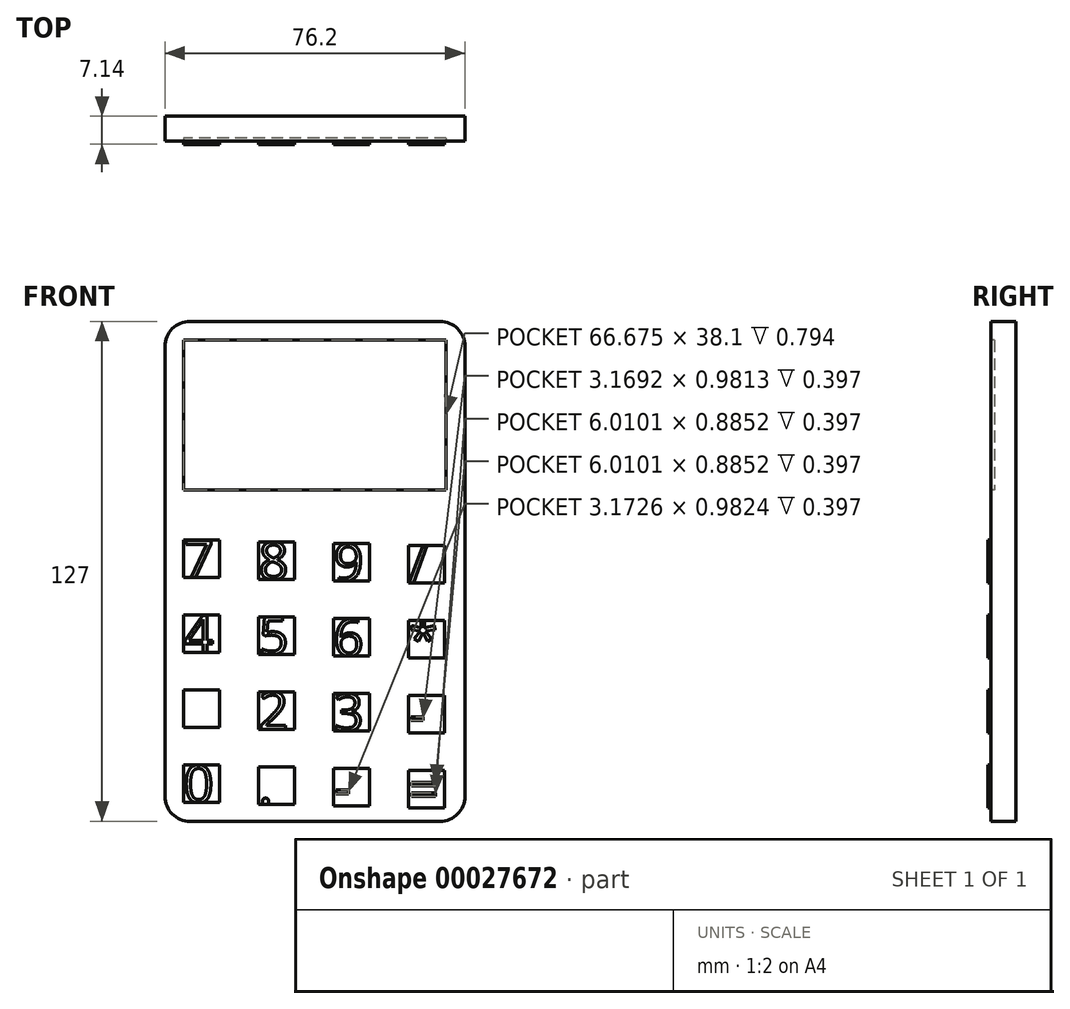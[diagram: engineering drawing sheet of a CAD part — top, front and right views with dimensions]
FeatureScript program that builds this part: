
annotation { "Feature Type Name" : "Feature", "Feature Type Description" : "" }
export const myFeature = defineFeature(function(context is Context, id is Id, definition is map)
    precondition{}
    {
        {
            var Q0;
            Q0=qCreatedBy(makeId("Front.planeOp"),FACE);
            var sketch = newSketch(context, id + "F0", { "sketchPlane" : qUnion([Q0])});
            skArc(sketch, "E0", {"start": v(-46, -23.23) * mm, "mid": v(-44.15, -27.72) * mm, "end": v(-39.66, -29.58) * mm});
            skArc(sketch, "E1", {"start": v(-39.66, 97.42) * mm, "mid": v(-44.15, 95.56) * mm, "end": v(-46, 91.07) * mm});
            skArc(sketch, "E2", {"start": v(30.2, 91.07) * mm, "mid": v(28.33, 95.56) * mm, "end": v(23.84, 97.42) * mm});
            skArc(sketch, "E3", {"start": v(23.84, -29.58) * mm, "mid": v(28.33, -27.72) * mm, "end": v(30.2, -23.23) * mm});
            skLineSegment(sketch, "E4", {"start": v(30.2, -23.23) * mm, "end": v(30.2, 91.07) * mm});
            skLineSegment(sketch, "E5", {"start": v(23.84, -29.58) * mm, "end": v(-39.66, -29.58) * mm});
            skLineSegment(sketch, "E6", {"start": v(23.84, 97.42) * mm, "end": v(-39.66, 97.42) * mm});
            skLineSegment(sketch, "E7", {"start": v(-46, -23.23) * mm, "end": v(-46, 91.07) * mm});
            skLineSegment(sketch, "E8.rect.bottom", {"start": v(25.43, 92.66) * mm, "end": v(-41.24, 92.66) * mm});
            skLineSegment(sketch, "E8.rect.top", {"start": v(25.43, 54.56) * mm, "end": v(-41.24, 54.56) * mm});
            skLineSegment(sketch, "E8.rect.left", {"start": v(25.43, 92.66) * mm, "end": v(25.43, 54.56) * mm});
            skLineSegment(sketch, "E8.rect.right", {"start": v(-41.24, 92.66) * mm, "end": v(-41.24, 54.56) * mm});
            skPoint(sketch, "E8.rect.middle", {"position": v(-7.9, 73.6) * mm});
            skLineSegment(sketch, "E9.bottom", {"start": v(-41.24, -24.82) * mm, "end": v(-32.08, -24.82) * mm});
            skLineSegment(sketch, "E9.top", {"start": v(-41.24, -15.3) * mm, "end": v(-32.08, -15.3) * mm});
            skLineSegment(sketch, "E9.left", {"start": v(-41.24, -24.82) * mm, "end": v(-41.24, -15.3) * mm});
            skLineSegment(sketch, "E9.right", {"start": v(-32.08, -24.82) * mm, "end": v(-32.08, -15.3) * mm});
            skLineSegment(sketch, "E10.0.1.0", {"start": v(-41.24, 3.76) * mm, "end": v(-32.08, 3.76) * mm});
            skLineSegment(sketch, "E10.0.1.1", {"start": v(-41.24, -5.77) * mm, "end": v(-41.24, 3.76) * mm});
            skLineSegment(sketch, "E10.0.1.2", {"start": v(-41.24, -5.77) * mm, "end": v(-32.08, -5.77) * mm});
            skLineSegment(sketch, "E10.0.1.3", {"start": v(-32.08, -5.77) * mm, "end": v(-32.08, 3.76) * mm});
            skLineSegment(sketch, "E10.0.2.0", {"start": v(-41.24, 22.8) * mm, "end": v(-32.08, 22.8) * mm});
            skLineSegment(sketch, "E10.0.2.1", {"start": v(-41.24, 13.28) * mm, "end": v(-41.24, 22.8) * mm});
            skLineSegment(sketch, "E10.0.2.2", {"start": v(-41.24, 13.28) * mm, "end": v(-32.08, 13.28) * mm});
            skLineSegment(sketch, "E10.0.2.3", {"start": v(-32.08, 13.28) * mm, "end": v(-32.08, 22.8) * mm});
            skLineSegment(sketch, "E10.0.3.0", {"start": v(-41.24, 41.86) * mm, "end": v(-32.08, 41.86) * mm});
            skLineSegment(sketch, "E10.0.3.1", {"start": v(-41.24, 32.33) * mm, "end": v(-41.24, 41.86) * mm});
            skLineSegment(sketch, "E10.0.3.2", {"start": v(-41.24, 32.33) * mm, "end": v(-32.08, 32.33) * mm});
            skLineSegment(sketch, "E10.0.3.3", {"start": v(-32.08, 32.33) * mm, "end": v(-32.08, 41.86) * mm});
            skLineSegment(sketch, "E10.1.0.0", {"start": v(-22.2, -15.73) * mm, "end": v(-13.03, -15.73) * mm});
            skLineSegment(sketch, "E10.1.0.1", {"start": v(-22.2, -25.25) * mm, "end": v(-22.2, -15.73) * mm});
            skLineSegment(sketch, "E10.1.0.2", {"start": v(-22.2, -25.25) * mm, "end": v(-13.03, -25.25) * mm});
            skLineSegment(sketch, "E10.1.0.3", {"start": v(-13.03, -25.25) * mm, "end": v(-13.03, -15.73) * mm});
            skLineSegment(sketch, "E10.1.1.0", {"start": v(-22.2, 3.32) * mm, "end": v(-13.03, 3.32) * mm});
            skLineSegment(sketch, "E10.1.1.1", {"start": v(-22.2, -6.2) * mm, "end": v(-22.2, 3.32) * mm});
            skLineSegment(sketch, "E10.1.1.2", {"start": v(-22.2, -6.2) * mm, "end": v(-13.03, -6.2) * mm});
            skLineSegment(sketch, "E10.1.1.3", {"start": v(-13.03, -6.2) * mm, "end": v(-13.03, 3.32) * mm});
            skLineSegment(sketch, "E10.1.2.0", {"start": v(-22.2, 22.37) * mm, "end": v(-13.03, 22.37) * mm});
            skLineSegment(sketch, "E10.1.2.1", {"start": v(-22.2, 12.85) * mm, "end": v(-22.2, 22.37) * mm});
            skLineSegment(sketch, "E10.1.2.2", {"start": v(-22.2, 12.85) * mm, "end": v(-13.03, 12.85) * mm});
            skLineSegment(sketch, "E10.1.2.3", {"start": v(-13.03, 12.85) * mm, "end": v(-13.03, 22.37) * mm});
            skLineSegment(sketch, "E10.1.3.0", {"start": v(-22.2, 41.42) * mm, "end": v(-13.03, 41.42) * mm});
            skLineSegment(sketch, "E10.1.3.1", {"start": v(-22.2, 31.9) * mm, "end": v(-22.2, 41.42) * mm});
            skLineSegment(sketch, "E10.1.3.2", {"start": v(-22.2, 31.9) * mm, "end": v(-13.03, 31.9) * mm});
            skLineSegment(sketch, "E10.1.3.3", {"start": v(-13.03, 31.9) * mm, "end": v(-13.03, 41.42) * mm});
            skLineSegment(sketch, "E10.2.0.0", {"start": v(-3.15, -16.16) * mm, "end": v(6.02, -16.16) * mm});
            skLineSegment(sketch, "E10.2.0.1", {"start": v(-3.15, -25.68) * mm, "end": v(-3.15, -16.16) * mm});
            skLineSegment(sketch, "E10.2.0.2", {"start": v(-3.15, -25.68) * mm, "end": v(6.02, -25.68) * mm});
            skLineSegment(sketch, "E10.2.0.3", {"start": v(6.02, -25.68) * mm, "end": v(6.02, -16.16) * mm});
            skLineSegment(sketch, "E10.2.1.0", {"start": v(-3.15, 2.9) * mm, "end": v(6.02, 2.9) * mm});
            skLineSegment(sketch, "E10.2.1.1", {"start": v(-3.15, -6.63) * mm, "end": v(-3.15, 2.9) * mm});
            skLineSegment(sketch, "E10.2.1.2", {"start": v(-3.15, -6.63) * mm, "end": v(6.02, -6.63) * mm});
            skLineSegment(sketch, "E10.2.1.3", {"start": v(6.02, -6.63) * mm, "end": v(6.02, 2.9) * mm});
            skLineSegment(sketch, "E10.2.2.0", {"start": v(-3.15, 21.94) * mm, "end": v(6.02, 21.94) * mm});
            skLineSegment(sketch, "E10.2.2.1", {"start": v(-3.15, 12.42) * mm, "end": v(-3.15, 21.94) * mm});
            skLineSegment(sketch, "E10.2.2.2", {"start": v(-3.15, 12.42) * mm, "end": v(6.02, 12.42) * mm});
            skLineSegment(sketch, "E10.2.2.3", {"start": v(6.02, 12.42) * mm, "end": v(6.02, 21.94) * mm});
            skLineSegment(sketch, "E10.2.3.0", {"start": v(-3.15, 41) * mm, "end": v(6.02, 41) * mm});
            skLineSegment(sketch, "E10.2.3.1", {"start": v(-3.15, 31.47) * mm, "end": v(-3.15, 41) * mm});
            skLineSegment(sketch, "E10.2.3.2", {"start": v(-3.15, 31.47) * mm, "end": v(6.02, 31.47) * mm});
            skLineSegment(sketch, "E10.2.3.3", {"start": v(6.02, 31.47) * mm, "end": v(6.02, 41) * mm});
            skLineSegment(sketch, "E10.3.0.0", {"start": v(15.9, -16.59) * mm, "end": v(25.06, -16.59) * mm});
            skLineSegment(sketch, "E10.3.0.1", {"start": v(15.9, -26.11) * mm, "end": v(15.9, -16.59) * mm});
            skLineSegment(sketch, "E10.3.0.2", {"start": v(15.9, -26.11) * mm, "end": v(25.06, -26.11) * mm});
            skLineSegment(sketch, "E10.3.0.3", {"start": v(25.06, -26.11) * mm, "end": v(25.06, -16.59) * mm});
            skLineSegment(sketch, "E10.3.1.0", {"start": v(15.9, 2.46) * mm, "end": v(25.06, 2.46) * mm});
            skLineSegment(sketch, "E10.3.1.1", {"start": v(15.9, -7.06) * mm, "end": v(15.9, 2.46) * mm});
            skLineSegment(sketch, "E10.3.1.2", {"start": v(15.9, -7.06) * mm, "end": v(25.06, -7.06) * mm});
            skLineSegment(sketch, "E10.3.1.3", {"start": v(25.06, -7.06) * mm, "end": v(25.06, 2.46) * mm});
            skLineSegment(sketch, "E10.3.2.0", {"start": v(15.9, 21.51) * mm, "end": v(25.06, 21.51) * mm});
            skLineSegment(sketch, "E10.3.2.1", {"start": v(15.9, 11.99) * mm, "end": v(15.9, 21.51) * mm});
            skLineSegment(sketch, "E10.3.2.2", {"start": v(15.9, 11.99) * mm, "end": v(25.06, 11.99) * mm});
            skLineSegment(sketch, "E10.3.2.3", {"start": v(25.06, 11.99) * mm, "end": v(25.06, 21.51) * mm});
            skLineSegment(sketch, "E10.3.3.0", {"start": v(15.9, 40.56) * mm, "end": v(25.06, 40.56) * mm});
            skLineSegment(sketch, "E10.3.3.1", {"start": v(15.9, 31.04) * mm, "end": v(15.9, 40.56) * mm});
            skLineSegment(sketch, "E10.3.3.2", {"start": v(15.9, 31.04) * mm, "end": v(25.06, 31.04) * mm});
            skLineSegment(sketch, "E10.3.3.3", {"start": v(25.06, 31.04) * mm, "end": v(25.06, 40.56) * mm});
            skLineSegment(sketch, "E10.direction1", {"start": v(-41.24, -15.3) * mm, "end": v(-22.2, -15.73) * mm, "construction": true});
            skLineSegment(sketch, "E10.direction2", {"start": v(-41.24, -15.3) * mm, "end": v(-41.24, 3.76) * mm, "construction": true});
            skSolve(sketch);
        }
        {
            var Q0;
            Q0 = qSketchRegion(id + "F0", true);
            var Q1;
            Q1=makeQuery(id+"F0.imprint","IMPRINT",FACE,{"disambiguationData":[TD([[makeQuery(id+"F0.imprint","IMPRINT",EDGE,{"derivedFrom":sQuery(id+"F0.wireOp",EDGE,"E8.rect.bottom")}),1.0]])]});
            extrude(context, id + "F1", {"entities" : qUnion([Q0, Q1]), "depth" : 6.35 * mm});
        }
        {
            var Q0;
            Q0=makeQuery(id+"F0.imprint","IMPRINT",FACE,{"disambiguationData":[TD([[makeQuery(id+"F0.imprint","IMPRINT",EDGE,{"derivedFrom":sQuery(id+"F0.wireOp",EDGE,"E10.0.3.0")}),-1.0]])]});
            var Q1;
            Q1=makeQuery(id+"F0.imprint","IMPRINT",FACE,{"disambiguationData":[TD([[makeQuery(id+"F0.imprint","IMPRINT",EDGE,{"derivedFrom":sQuery(id+"F0.wireOp",EDGE,"E10.0.2.0")}),-1.0]])]});
            var Q2;
            Q2=makeQuery(id+"F0.imprint","IMPRINT",FACE,{"disambiguationData":[TD([[makeQuery(id+"F0.imprint","IMPRINT",EDGE,{"derivedFrom":sQuery(id+"F0.wireOp",EDGE,"E10.0.1.0")}),-1.0]])]});
            var Q3;
            Q3=makeQuery(id+"F0.imprint","IMPRINT",FACE,{"disambiguationData":[TD([[makeQuery(id+"F0.imprint","IMPRINT",EDGE,{"derivedFrom":sQuery(id+"F0.wireOp",EDGE,"E9.bottom")}),1.0]])]});
            var Q4;
            Q4=makeQuery(id+"F0.imprint","IMPRINT",FACE,{"disambiguationData":[TD([[makeQuery(id+"F0.imprint","IMPRINT",EDGE,{"derivedFrom":sQuery(id+"F0.wireOp",EDGE,"E10.1.0.0")}),-1.0]])]});
            var Q5;
            Q5=makeQuery(id+"F0.imprint","IMPRINT",FACE,{"disambiguationData":[TD([[makeQuery(id+"F0.imprint","IMPRINT",EDGE,{"derivedFrom":sQuery(id+"F0.wireOp",EDGE,"E10.1.1.0")}),-1.0]])]});
            var Q6;
            Q6=makeQuery(id+"F0.imprint","IMPRINT",FACE,{"disambiguationData":[TD([[makeQuery(id+"F0.imprint","IMPRINT",EDGE,{"derivedFrom":sQuery(id+"F0.wireOp",EDGE,"E10.1.2.0")}),-1.0]])]});
            var Q7;
            Q7=makeQuery(id+"F0.imprint","IMPRINT",FACE,{"disambiguationData":[TD([[makeQuery(id+"F0.imprint","IMPRINT",EDGE,{"derivedFrom":sQuery(id+"F0.wireOp",EDGE,"E10.1.3.0")}),-1.0]])]});
            var Q8;
            Q8=makeQuery(id+"F0.imprint","IMPRINT",FACE,{"disambiguationData":[TD([[makeQuery(id+"F0.imprint","IMPRINT",EDGE,{"derivedFrom":sQuery(id+"F0.wireOp",EDGE,"E10.2.3.0")}),-1.0]])]});
            var Q9;
            Q9=makeQuery(id+"F0.imprint","IMPRINT",FACE,{"disambiguationData":[TD([[makeQuery(id+"F0.imprint","IMPRINT",EDGE,{"derivedFrom":sQuery(id+"F0.wireOp",EDGE,"E10.2.2.0")}),-1.0]])]});
            var Q10;
            Q10=makeQuery(id+"F0.imprint","IMPRINT",FACE,{"disambiguationData":[TD([[makeQuery(id+"F0.imprint","IMPRINT",EDGE,{"derivedFrom":sQuery(id+"F0.wireOp",EDGE,"E10.2.1.0")}),-1.0]])]});
            var Q11;
            Q11=makeQuery(id+"F0.imprint","IMPRINT",FACE,{"disambiguationData":[TD([[makeQuery(id+"F0.imprint","IMPRINT",EDGE,{"derivedFrom":sQuery(id+"F0.wireOp",EDGE,"E10.2.0.0")}),-1.0]])]});
            var Q12;
            Q12=makeQuery(id+"F0.imprint","IMPRINT",FACE,{"disambiguationData":[TD([[makeQuery(id+"F0.imprint","IMPRINT",EDGE,{"derivedFrom":sQuery(id+"F0.wireOp",EDGE,"E10.3.3.0")}),-1.0]])]});
            var Q13;
            Q13=makeQuery(id+"F0.imprint","IMPRINT",FACE,{"disambiguationData":[TD([[makeQuery(id+"F0.imprint","IMPRINT",EDGE,{"derivedFrom":sQuery(id+"F0.wireOp",EDGE,"E10.3.2.0")}),-1.0]])]});
            var Q14;
            Q14=makeQuery(id+"F0.imprint","IMPRINT",FACE,{"disambiguationData":[TD([[makeQuery(id+"F0.imprint","IMPRINT",EDGE,{"derivedFrom":sQuery(id+"F0.wireOp",EDGE,"E10.3.1.0")}),-1.0]])]});
            var Q15;
            Q15=makeQuery(id+"F0.imprint","IMPRINT",FACE,{"disambiguationData":[TD([[makeQuery(id+"F0.imprint","IMPRINT",EDGE,{"derivedFrom":sQuery(id+"F0.wireOp",EDGE,"E10.3.0.0")}),-1.0]])]});
            extrude(context, id + "F2", {"entities" : qUnion([Q0, Q1, Q2, Q3, Q4, Q5, Q6, Q7, Q8, Q9, Q10, Q11, Q12, Q13, Q14, Q15]), "operationType" : NewBodyOperationType.ADD, "flatOperationType" : FlatOperationType.REMOVE, "offsetDistance" : 25.4 * mm, "depth" : 7.14 * mm, "domain" : OperationDomain.MODEL});
        }
        {
            var Q0;
            Q0=makeQuery(id+"F1.opExtrude","CAP_FACE",FACE,{"disambiguationData":[OSD([sQuery(id+"F0.wireOp",EDGE,"E0"),sQuery(id+"F0.wireOp",EDGE,"E1"),sQuery(id+"F0.wireOp",EDGE,"E2"),sQuery(id+"F0.wireOp",EDGE,"E3"),sQuery(id+"F0.wireOp",EDGE,"E4"),sQuery(id+"F0.wireOp",EDGE,"E5"),sQuery(id+"F0.wireOp",EDGE,"E6"),sQuery(id+"F0.wireOp",EDGE,"E7"),sQuery(id+"F0.wireOp",EDGE,"E9.bottom"),sQuery(id+"F0.wireOp",EDGE,"E9.top"),sQuery(id+"F0.wireOp",EDGE,"E9.left"),sQuery(id+"F0.wireOp",EDGE,"E9.right"),sQuery(id+"F0.wireOp",EDGE,"E10.0.1.0"),sQuery(id+"F0.wireOp",EDGE,"E10.0.1.1"),sQuery(id+"F0.wireOp",EDGE,"E10.0.1.2"),sQuery(id+"F0.wireOp",EDGE,"E10.0.1.3"),sQuery(id+"F0.wireOp",EDGE,"E10.0.2.0"),sQuery(id+"F0.wireOp",EDGE,"E10.0.2.1"),sQuery(id+"F0.wireOp",EDGE,"E10.0.2.2"),sQuery(id+"F0.wireOp",EDGE,"E10.0.2.3"),sQuery(id+"F0.wireOp",EDGE,"E10.0.3.0"),sQuery(id+"F0.wireOp",EDGE,"E10.0.3.1"),sQuery(id+"F0.wireOp",EDGE,"E10.0.3.2"),sQuery(id+"F0.wireOp",EDGE,"E10.0.3.3"),sQuery(id+"F0.wireOp",EDGE,"E10.1.0.0"),sQuery(id+"F0.wireOp",EDGE,"E10.1.0.1"),sQuery(id+"F0.wireOp",EDGE,"E10.1.0.2"),sQuery(id+"F0.wireOp",EDGE,"E10.1.0.3"),sQuery(id+"F0.wireOp",EDGE,"E10.1.1.0"),sQuery(id+"F0.wireOp",EDGE,"E10.1.1.1"),sQuery(id+"F0.wireOp",EDGE,"E10.1.1.2"),sQuery(id+"F0.wireOp",EDGE,"E10.1.1.3"),sQuery(id+"F0.wireOp",EDGE,"E10.1.2.0"),sQuery(id+"F0.wireOp",EDGE,"E10.1.2.1"),sQuery(id+"F0.wireOp",EDGE,"E10.1.2.2"),sQuery(id+"F0.wireOp",EDGE,"E10.1.2.3"),sQuery(id+"F0.wireOp",EDGE,"E10.1.3.0"),sQuery(id+"F0.wireOp",EDGE,"E10.1.3.1"),sQuery(id+"F0.wireOp",EDGE,"E10.1.3.2"),sQuery(id+"F0.wireOp",EDGE,"E10.1.3.3"),sQuery(id+"F0.wireOp",EDGE,"E10.2.0.0"),sQuery(id+"F0.wireOp",EDGE,"E10.2.0.1"),sQuery(id+"F0.wireOp",EDGE,"E10.2.0.2"),sQuery(id+"F0.wireOp",EDGE,"E10.2.0.3"),sQuery(id+"F0.wireOp",EDGE,"E10.2.1.0"),sQuery(id+"F0.wireOp",EDGE,"E10.2.1.1"),sQuery(id+"F0.wireOp",EDGE,"E10.2.1.2"),sQuery(id+"F0.wireOp",EDGE,"E10.2.1.3"),sQuery(id+"F0.wireOp",EDGE,"E10.2.2.0"),sQuery(id+"F0.wireOp",EDGE,"E10.2.2.1"),sQuery(id+"F0.wireOp",EDGE,"E10.2.2.2"),sQuery(id+"F0.wireOp",EDGE,"E10.2.2.3"),sQuery(id+"F0.wireOp",EDGE,"E10.2.3.0"),sQuery(id+"F0.wireOp",EDGE,"E10.2.3.1"),sQuery(id+"F0.wireOp",EDGE,"E10.2.3.2"),sQuery(id+"F0.wireOp",EDGE,"E10.2.3.3"),sQuery(id+"F0.wireOp",EDGE,"E10.3.0.0"),sQuery(id+"F0.wireOp",EDGE,"E10.3.0.1"),sQuery(id+"F0.wireOp",EDGE,"E10.3.0.2"),sQuery(id+"F0.wireOp",EDGE,"E10.3.0.3"),sQuery(id+"F0.wireOp",EDGE,"E10.3.1.0"),sQuery(id+"F0.wireOp",EDGE,"E10.3.1.1"),sQuery(id+"F0.wireOp",EDGE,"E10.3.1.2"),sQuery(id+"F0.wireOp",EDGE,"E10.3.1.3"),sQuery(id+"F0.wireOp",EDGE,"E10.3.2.0"),sQuery(id+"F0.wireOp",EDGE,"E10.3.2.1"),sQuery(id+"F0.wireOp",EDGE,"E10.3.2.2"),sQuery(id+"F0.wireOp",EDGE,"E10.3.2.3"),sQuery(id+"F0.wireOp",EDGE,"E10.3.3.0"),sQuery(id+"F0.wireOp",EDGE,"E10.3.3.1"),sQuery(id+"F0.wireOp",EDGE,"E10.3.3.2"),sQuery(id+"F0.wireOp",EDGE,"E10.3.3.3")])],"isStart":false});
            var sketch = newSketch(context, id + "F3", { "sketchPlane" : qUnion([Q0])});
            skLineSegment(sketch, "E11.0", {"start": v(25.43, 92.66) * mm, "end": v(25.43, 54.56) * mm});
            skLineSegment(sketch, "E12.0", {"start": v(25.43, 92.66) * mm, "end": v(-41.24, 92.66) * mm});
            skLineSegment(sketch, "E13.0.0", {"start": v(-46, 91.07) * mm, "end": v(-46, -23.23) * mm});
            skArc(sketch, "E13.0.1", {"start": v(-46, -23.23) * mm, "mid": v(-44.15, -27.72) * mm, "end": v(-39.66, -29.58) * mm});
            skLineSegment(sketch, "E13.0.2", {"start": v(-39.66, -29.58) * mm, "end": v(23.84, -29.58) * mm});
            skArc(sketch, "E13.0.3", {"start": v(23.84, -29.58) * mm, "mid": v(28.33, -27.72) * mm, "end": v(30.2, -23.23) * mm});
            skLineSegment(sketch, "E13.0.4", {"start": v(30.2, -23.23) * mm, "end": v(30.2, 91.07) * mm});
            skArc(sketch, "E13.0.5", {"start": v(30.2, 91.07) * mm, "mid": v(28.33, 95.56) * mm, "end": v(23.84, 97.42) * mm});
            skLineSegment(sketch, "E13.0.6", {"start": v(23.84, 97.42) * mm, "end": v(-39.66, 97.42) * mm});
            skArc(sketch, "E13.0.7", {"start": v(-39.66, 97.42) * mm, "mid": v(-44.15, 95.56) * mm, "end": v(-46, 91.07) * mm});
            skLineSegment(sketch, "E14.0", {"start": v(-41.24, 92.66) * mm, "end": v(-41.24, 54.56) * mm});
            skLineSegment(sketch, "E15.0", {"start": v(25.43, 54.56) * mm, "end": v(-41.24, 54.56) * mm});
            skSolve(sketch);
        }
        {
            var Q0;
            Q0=makeQuery(id+"F3.imprint","IMPRINT",FACE,{"disambiguationData":[TD([[makeQuery(id+"F3.imprint","IMPRINT",EDGE,{"derivedFrom":sQuery(id+"F3.wireOp",EDGE,"E12.0")}),1.0]])]});
            extrude(context, id + "F4", {"entities" : qUnion([Q0]), "operationType" : NewBodyOperationType.REMOVE, "oppositeDirection" : true, "depth" : 0.8 * mm});
        }
        {
            var Q0;
            Q0=makeQuery(id+"F2.opExtrude","CAP_FACE",FACE,{"disambiguationData":[OSD([sQuery(id+"F0.wireOp",EDGE,"E10.0.3.0"),sQuery(id+"F0.wireOp",EDGE,"E10.0.3.1"),sQuery(id+"F0.wireOp",EDGE,"E10.0.3.2"),sQuery(id+"F0.wireOp",EDGE,"E10.0.3.3")])],"isStart":false});
            var sketch = newSketch(context, id + "F5", { "sketchPlane" : qUnion([Q0])});
            skLineSegment(sketch, "E16.0.0", {"start": v(-13.03, 41.42) * mm, "end": v(-22.2, 41.42) * mm});
            skLineSegment(sketch, "E16.0.1", {"start": v(-22.2, 41.42) * mm, "end": v(-22.2, 31.9) * mm});
            skLineSegment(sketch, "E16.0.2", {"start": v(-22.2, 31.9) * mm, "end": v(-13.03, 31.9) * mm});
            skLineSegment(sketch, "E16.0.3", {"start": v(-13.03, 31.9) * mm, "end": v(-13.03, 41.42) * mm});
            skLineSegment(sketch, "E17.0.0", {"start": v(6.02, 41) * mm, "end": v(-3.15, 41) * mm});
            skLineSegment(sketch, "E17.0.1", {"start": v(-3.15, 41) * mm, "end": v(-3.15, 31.47) * mm});
            skLineSegment(sketch, "E17.0.2", {"start": v(-3.15, 31.47) * mm, "end": v(6.02, 31.47) * mm});
            skLineSegment(sketch, "E17.0.3", {"start": v(6.02, 31.47) * mm, "end": v(6.02, 41) * mm});
            skLineSegment(sketch, "E18.0.0", {"start": v(25.06, 40.56) * mm, "end": v(15.9, 40.56) * mm});
            skLineSegment(sketch, "E18.0.1", {"start": v(15.9, 40.56) * mm, "end": v(15.9, 31.04) * mm});
            skLineSegment(sketch, "E18.0.2", {"start": v(15.9, 31.04) * mm, "end": v(25.06, 31.04) * mm});
            skLineSegment(sketch, "E18.0.3", {"start": v(25.06, 31.04) * mm, "end": v(25.06, 40.56) * mm});
            skLineSegment(sketch, "E19.0.0", {"start": v(25.06, 21.51) * mm, "end": v(15.9, 21.51) * mm});
            skLineSegment(sketch, "E19.0.1", {"start": v(15.9, 21.51) * mm, "end": v(15.9, 11.99) * mm});
            skLineSegment(sketch, "E19.0.2", {"start": v(15.9, 11.99) * mm, "end": v(25.06, 11.99) * mm});
            skLineSegment(sketch, "E19.0.3", {"start": v(25.06, 11.99) * mm, "end": v(25.06, 21.51) * mm});
            skLineSegment(sketch, "E20.0.0", {"start": v(6.02, 21.94) * mm, "end": v(-3.15, 21.94) * mm});
            skLineSegment(sketch, "E20.0.1", {"start": v(-3.15, 21.94) * mm, "end": v(-3.15, 12.42) * mm});
            skLineSegment(sketch, "E20.0.2", {"start": v(-3.15, 12.42) * mm, "end": v(6.02, 12.42) * mm});
            skLineSegment(sketch, "E20.0.3", {"start": v(6.02, 12.42) * mm, "end": v(6.02, 21.94) * mm});
            skLineSegment(sketch, "E21.0.0", {"start": v(-13.03, 22.37) * mm, "end": v(-22.2, 22.37) * mm});
            skLineSegment(sketch, "E21.0.1", {"start": v(-22.2, 22.37) * mm, "end": v(-22.2, 12.85) * mm});
            skLineSegment(sketch, "E21.0.2", {"start": v(-22.2, 12.85) * mm, "end": v(-13.03, 12.85) * mm});
            skLineSegment(sketch, "E21.0.3", {"start": v(-13.03, 12.85) * mm, "end": v(-13.03, 22.37) * mm});
            skLineSegment(sketch, "E22.0.0", {"start": v(-32.08, 22.8) * mm, "end": v(-41.24, 22.8) * mm});
            skLineSegment(sketch, "E22.0.1", {"start": v(-41.24, 22.8) * mm, "end": v(-41.24, 13.28) * mm});
            skLineSegment(sketch, "E22.0.2", {"start": v(-41.24, 13.28) * mm, "end": v(-32.08, 13.28) * mm});
            skLineSegment(sketch, "E22.0.3", {"start": v(-32.08, 13.28) * mm, "end": v(-32.08, 22.8) * mm});
            skLineSegment(sketch, "E23.0.0", {"start": v(-32.08, 3.76) * mm, "end": v(-41.24, 3.76) * mm});
            skLineSegment(sketch, "E23.0.1", {"start": v(-41.24, 3.76) * mm, "end": v(-41.24, -5.77) * mm});
            skLineSegment(sketch, "E23.0.2", {"start": v(-41.24, -5.77) * mm, "end": v(-32.08, -5.77) * mm});
            skLineSegment(sketch, "E23.0.3", {"start": v(-32.08, -5.77) * mm, "end": v(-32.08, 3.76) * mm});
            skLineSegment(sketch, "E24.0.0", {"start": v(-13.03, 3.32) * mm, "end": v(-22.2, 3.32) * mm});
            skLineSegment(sketch, "E24.0.1", {"start": v(-22.2, 3.32) * mm, "end": v(-22.2, -6.2) * mm});
            skLineSegment(sketch, "E24.0.2", {"start": v(-22.2, -6.2) * mm, "end": v(-13.03, -6.2) * mm});
            skLineSegment(sketch, "E24.0.3", {"start": v(-13.03, -6.2) * mm, "end": v(-13.03, 3.32) * mm});
            skText(sketch, "E25", { "text": "7", "fontName": "OpenSans-Regular.ttf"});
            skText(sketch, "E26", { "text": "8", "fontName": "OpenSans-Regular.ttf"});
            skText(sketch, "E27", { "text": "9", "fontName": "OpenSans-Regular.ttf"});
            skText(sketch, "E28", { "text": "/", "fontName": "OpenSans-Regular.ttf"});
            skText(sketch, "E29", { "text": "4", "fontName": "OpenSans-Regular.ttf"});
            skText(sketch, "E30", { "text": "5", "fontName": "OpenSans-Regular.ttf"});
            skText(sketch, "E31", { "text": "6", "fontName": "OpenSans-Regular.ttf"});
            skText(sketch, "E32", { "text": "*", "fontName": "OpenSans-Regular.ttf"});
            skText(sketch, "E33", { "text": "1", "fontName": "OpenSans-Regular.ttf"});
            skText(sketch, "E34", { "text": "2", "fontName": "OpenSans-Regular.ttf"});
            skLineSegment(sketch, "E35.0.0", {"start": v(6.02, 2.9) * mm, "end": v(-3.15, 2.9) * mm});
            skLineSegment(sketch, "E35.0.1", {"start": v(-3.15, 2.9) * mm, "end": v(-3.15, -6.63) * mm});
            skLineSegment(sketch, "E35.0.2", {"start": v(-3.15, -6.63) * mm, "end": v(6.02, -6.63) * mm});
            skLineSegment(sketch, "E35.0.3", {"start": v(6.02, -6.63) * mm, "end": v(6.02, 2.9) * mm});
            skLineSegment(sketch, "E36.0.0", {"start": v(25.06, 2.46) * mm, "end": v(15.9, 2.46) * mm});
            skLineSegment(sketch, "E36.0.1", {"start": v(15.9, 2.46) * mm, "end": v(15.9, -7.06) * mm});
            skLineSegment(sketch, "E36.0.2", {"start": v(15.9, -7.06) * mm, "end": v(25.06, -7.06) * mm});
            skLineSegment(sketch, "E36.0.3", {"start": v(25.06, -7.06) * mm, "end": v(25.06, 2.46) * mm});
            skLineSegment(sketch, "E37.0.0", {"start": v(25.06, -16.59) * mm, "end": v(15.9, -16.59) * mm});
            skLineSegment(sketch, "E37.0.1", {"start": v(15.9, -16.59) * mm, "end": v(15.9, -26.11) * mm});
            skLineSegment(sketch, "E37.0.2", {"start": v(15.9, -26.11) * mm, "end": v(25.06, -26.11) * mm});
            skLineSegment(sketch, "E37.0.3", {"start": v(25.06, -26.11) * mm, "end": v(25.06, -16.59) * mm});
            skLineSegment(sketch, "E38.0.0", {"start": v(6.02, -16.16) * mm, "end": v(-3.15, -16.16) * mm});
            skLineSegment(sketch, "E38.0.1", {"start": v(-3.15, -16.16) * mm, "end": v(-3.15, -25.68) * mm});
            skLineSegment(sketch, "E38.0.2", {"start": v(-3.15, -25.68) * mm, "end": v(6.02, -25.68) * mm});
            skLineSegment(sketch, "E38.0.3", {"start": v(6.02, -25.68) * mm, "end": v(6.02, -16.16) * mm});
            skLineSegment(sketch, "E39.0.0", {"start": v(-13.03, -15.73) * mm, "end": v(-22.2, -15.73) * mm});
            skLineSegment(sketch, "E39.0.1", {"start": v(-22.2, -15.73) * mm, "end": v(-22.2, -25.25) * mm});
            skLineSegment(sketch, "E39.0.2", {"start": v(-22.2, -25.25) * mm, "end": v(-13.03, -25.25) * mm});
            skLineSegment(sketch, "E39.0.3", {"start": v(-13.03, -25.25) * mm, "end": v(-13.03, -15.73) * mm});
            skLineSegment(sketch, "E40.0.0", {"start": v(-41.24, -15.3) * mm, "end": v(-41.24, -24.82) * mm});
            skLineSegment(sketch, "E40.0.1", {"start": v(-41.24, -24.82) * mm, "end": v(-32.08, -24.82) * mm});
            skLineSegment(sketch, "E40.0.2", {"start": v(-32.08, -24.82) * mm, "end": v(-32.08, -15.3) * mm});
            skLineSegment(sketch, "E40.0.3", {"start": v(-32.08, -15.3) * mm, "end": v(-41.24, -15.3) * mm});
            skText(sketch, "E41", { "text": "3", "fontName": "OpenSans-Regular.ttf"});
            skText(sketch, "E42", { "text": "-", "fontName": "OpenSans-Regular.ttf"});
            skText(sketch, "E43", { "text": "0", "fontName": "OpenSans-Regular.ttf"});
            skText(sketch, "E44", { "text": ".", "fontName": "OpenSans-Regular.ttf"});
            skText(sketch, "E45", { "text": "=", "fontName": "OpenSans-Regular.ttf"});
            skText(sketch, "E46", { "text": "-", "fontName": "OpenSans-Regular.ttf"});
            const initialGuessF5  = {"E25": [-0.04124, 0.03233, 1, 0, 0.00952], "E26": [-0.0222, 0.0319, 1, 0, 0.00952], "E27": [-0.00315, 0.03147, 1, 0, 0.00952], "E28": [0.0159, 0.03104, 1, 0, 0.00952], "E29": [-0.04124, 0.01328, 1, 0, 0.00952], "E30": [-0.0222, 0.01285, 1, 0, 0.00952], "E31": [-0.00315, 0.01242, 1, 0, 0.00952], "E32": [0.0159, 0.01199, 1, 0, 0.00952], "E33": [-0.04124, -0.00577, 1, 0, 0.00952], "E34": [-0.0222, -0.0062, 1, 0, 0.00953], "E41": [-0.00315, -0.00663, 1, 0, 0.00953], "E42": [0.0159, -0.00706, 1, 0, 0.00952], "E43": [-0.04124, -0.02482, 1, 0, 0.00952], "E44": [-0.0222, -0.02525, 1, 0, 0.00953], "E45": [0.0159, -0.02611, 1, 0, 0.00953], "E46": [-0.00315, -0.02568, 1, 0, 0.00953]};
            skSetInitialGuess(sketch, initialGuessF5);
            skSolve(sketch);
        }
        {
            var Q0;
            Q0=makeQuery(id+"F5.imprint","IMPRINT",FACE,{"disambiguationData":[TD([[makeQuery(id+"F5.imprint","IMPRINT",EDGE,{"derivedFrom":sQuery(id+"F5.wireOp",EDGE,"E25.sketch_text.stroke-0")}),-1.0]])]});
            var Q1;
            {var subQ5=sQuery(id+"F5.wireOp",EDGE,"E26.sketch_text.stroke-1");Q1=makeQuery(id+"F5.imprint","IMPRINT",FACE,{"disambiguationData":[TD([[makeQuery(id+"F5.imprint","IMPRINT",EDGE,{"derivedFrom":subQ5}),-1.0]])]});}
            var Q2;
            {var subQ7=sQuery(id+"F5.wireOp",EDGE,"E27.sketch_text.stroke-2");Q2=makeQuery(id+"F5.imprint","IMPRINT",FACE,{"disambiguationData":[TD([[makeQuery(id+"F5.imprint","IMPRINT",EDGE,{"derivedFrom":subQ7}),-1.0]])]});}
            var Q3;
            Q3=makeQuery(id+"F5.imprint","IMPRINT",FACE,{"disambiguationData":[TD([[makeQuery(id+"F5.imprint","IMPRINT",EDGE,{"derivedFrom":sQuery(id+"F5.wireOp",EDGE,"E28.sketch_text.stroke-0")}),-1.0]])]});
            var Q4;
            Q4=makeQuery(id+"F5.imprint","IMPRINT",FACE,{"disambiguationData":[TD([[makeQuery(id+"F5.imprint","IMPRINT",EDGE,{"derivedFrom":sQuery(id+"F5.wireOp",EDGE,"E29.sketch_text.stroke-0")}),-1.0]])]});
            var Q5;
            Q5=makeQuery(id+"F5.imprint","IMPRINT",FACE,{"disambiguationData":[TD([[makeQuery(id+"F5.imprint","IMPRINT",EDGE,{"derivedFrom":sQuery(id+"F5.wireOp",EDGE,"E30.sketch_text.stroke-0")}),-1.0]])]});
            var Q6;
            {var subQ5=sQuery(id+"F5.wireOp",EDGE,"E31.sketch_text.stroke-0");Q6=makeQuery(id+"F5.imprint","IMPRINT",FACE,{"disambiguationData":[TD([[makeQuery(id+"F5.imprint","IMPRINT",EDGE,{"derivedFrom":subQ5}),-1.0]])]});}
            var Q7;
            {var subQ4=sQuery(id+"F5.wireOp",EDGE,"E32.sketch_text.stroke-1");Q7=makeQuery(id+"F5.imprint","IMPRINT",FACE,{"disambiguationData":[TD([[makeQuery(id+"F5.imprint","IMPRINT",EDGE,{"derivedFrom":subQ4}),-1.0]])]});}
            var Q8;
            Q8=makeQuery(id+"F5.imprint","IMPRINT",FACE,{"disambiguationData":[TD([[makeQuery(id+"F5.imprint","IMPRINT",EDGE,{"derivedFrom":sQuery(id+"F5.wireOp",EDGE,"E33.sketch_text.stroke-0")}),-1.0]])]});
            var Q9;
            Q9=makeQuery(id+"F5.imprint","IMPRINT",FACE,{"disambiguationData":[TD([[makeQuery(id+"F5.imprint","IMPRINT",EDGE,{"derivedFrom":sQuery(id+"F5.wireOp",EDGE,"E34.sketch_text.stroke-0")}),-1.0]])]});
            var Q10;
            Q10=makeQuery(id+"F5.imprint","IMPRINT",FACE,{"disambiguationData":[TD([[makeQuery(id+"F5.imprint","IMPRINT",EDGE,{"derivedFrom":sQuery(id+"F5.wireOp",EDGE,"E41.sketch_text.stroke-0")}),-1.0]])]});
            var Q11;
            Q11=makeQuery(id+"F5.imprint","IMPRINT",FACE,{"disambiguationData":[TD([[makeQuery(id+"F5.imprint","IMPRINT",EDGE,{"derivedFrom":sQuery(id+"F5.wireOp",EDGE,"E42.sketch_text.stroke-0")}),-1.0]])]});
            var Q12;
            {var subQ9=sQuery(id+"F5.wireOp",EDGE,"E43.sketch_text.stroke-0");Q12=makeQuery(id+"F5.imprint","IMPRINT",FACE,{"disambiguationData":[TD([[makeQuery(id+"F5.imprint","IMPRINT",EDGE,{"derivedFrom":subQ9}),-1.0]])]});}
            var Q13;
            Q13=makeQuery(id+"F5.imprint","IMPRINT",FACE,{"disambiguationData":[TD([[makeQuery(id+"F5.imprint","IMPRINT",EDGE,{"derivedFrom":sQuery(id+"F5.wireOp",EDGE,"E44.sketch_text.stroke-0")}),-1.0]])]});
            var Q14;
            Q14=makeQuery(id+"F5.imprint","IMPRINT",FACE,{"disambiguationData":[TD([[makeQuery(id+"F5.imprint","IMPRINT",EDGE,{"derivedFrom":sQuery(id+"F5.wireOp",EDGE,"dd6d010b-a017-4a16-af01-4af9c69792f1.sketch_text.stroke-0")}),-1.0]])]});
            var Q15;
            Q15=makeQuery(id+"F5.imprint","IMPRINT",FACE,{"disambiguationData":[TD([[makeQuery(id+"F5.imprint","IMPRINT",EDGE,{"derivedFrom":sQuery(id+"F5.wireOp",EDGE,"dd6d010b-a017-4a16-af01-4af9c69792f1.sketch_text.stroke-14")}),-1.0]])]});
            var Q16;
            Q16=makeQuery(id+"F5.imprint","IMPRINT",FACE,{"disambiguationData":[TD([[makeQuery(id+"F5.imprint","IMPRINT",EDGE,{"derivedFrom":sQuery(id+"F5.wireOp",EDGE,"dd6d010b-a017-4a16-af01-4af9c69792f1.sketch_text.stroke-10")}),-1.0]])]});
            var Q17;
            Q17=makeQuery(id+"F5.imprint","IMPRINT",FACE,{"disambiguationData":[TD([[makeQuery(id+"F5.imprint","IMPRINT",EDGE,{"derivedFrom":sQuery(id+"F5.wireOp",EDGE,"E45.sketch_text.stroke-0")}),-1.0]])]});
            var Q18;
            Q18=makeQuery(id+"F5.imprint","IMPRINT",FACE,{"disambiguationData":[TD([[makeQuery(id+"F5.imprint","IMPRINT",EDGE,{"derivedFrom":sQuery(id+"F5.wireOp",EDGE,"E45.sketch_text.stroke-4")}),-1.0]])]});
            var Q19;
            Q19=makeQuery(id+"F5.imprint","IMPRINT",FACE,{"disambiguationData":[TD([[makeQuery(id+"F5.imprint","IMPRINT",EDGE,{"derivedFrom":sQuery(id+"F5.wireOp",EDGE,"E46.sketch_text.stroke-0")}),-1.0]])]});
            extrude(context, id + "F6", {"entities" : qUnion([Q0, Q1, Q2, Q3, Q4, Q5, Q6, Q7, Q8, Q9, Q10, Q11, Q12, Q13, Q14, Q15, Q16, Q17, Q18, Q19]), "operationType" : NewBodyOperationType.REMOVE, "oppositeDirection" : true, "depth" : 0.4 * mm});
        }
    });
